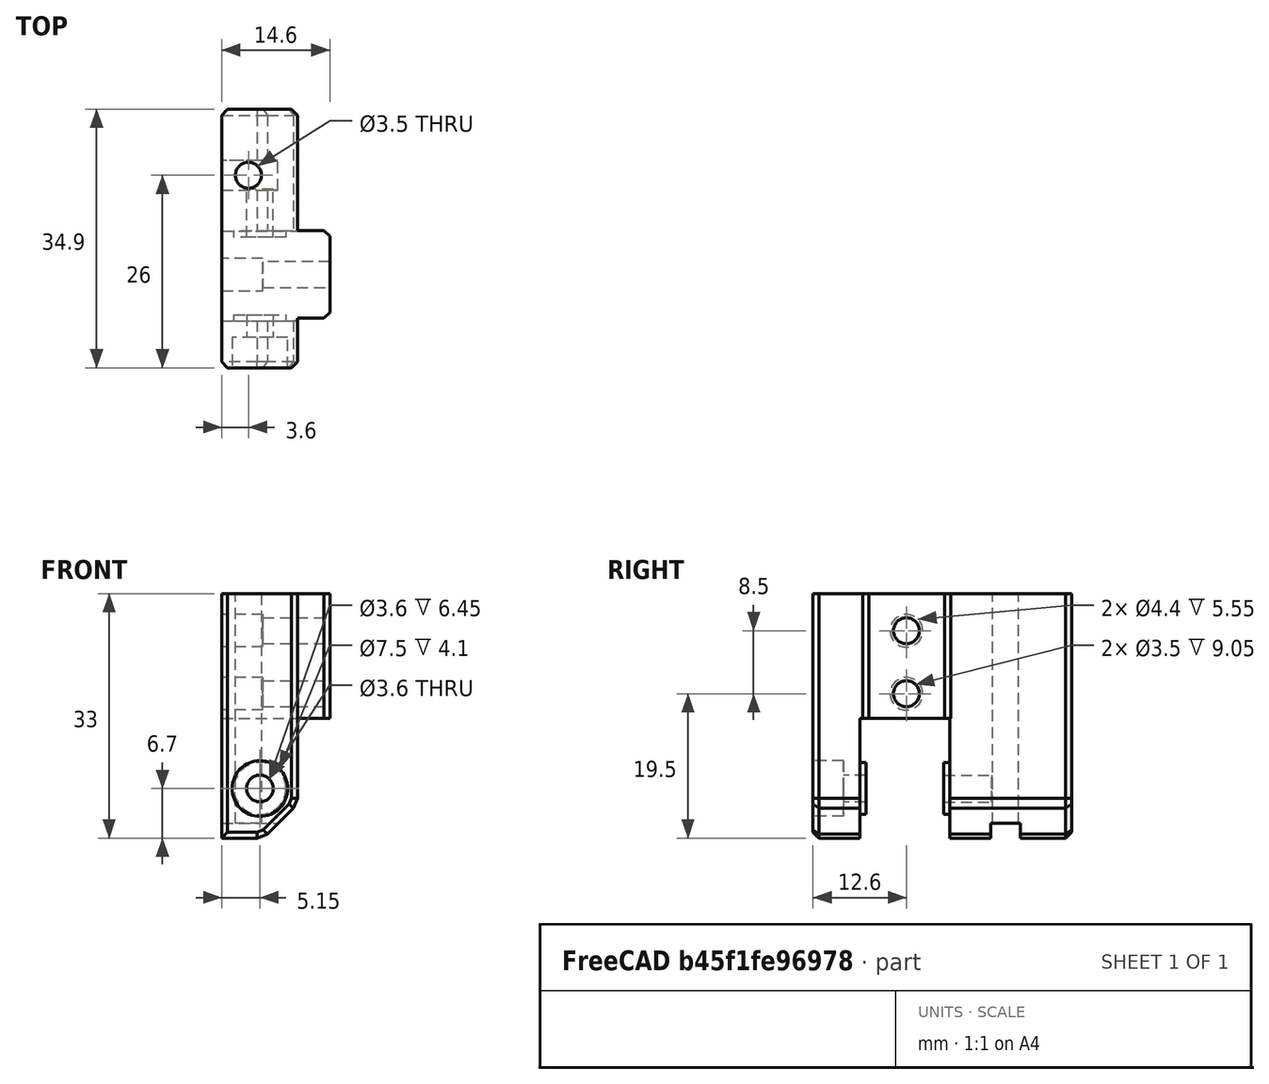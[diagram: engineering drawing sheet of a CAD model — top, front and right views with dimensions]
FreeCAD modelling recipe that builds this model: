
FCSTD DOCUMENT  (FreeCAD 1.0R38641 +468 (Git))
Label: k1_tensioner_right
License: All rights reserved
LicenseURL: https://en.wikipedia.org/wiki/All_rights_reserved
objects: Part::Feature×1, App::Link×1, PartDesign::FeatureBase×1, PartDesign::Body×1, App::Part×1
note: 4 computed .brp shape members not serialized (recipe doc carries the construction recipe); baked Part::Feature solids carry a one-line shape summary decoded from their .brp
EXTERNAL_REF file=cad_powge_pulley.FCStd obj=Part

FEATURE [Part::Feature] Part__Feature  label="step"
  shape: bbox 14.6 x 34.9 x 33 mm, 55 faces (baked)
FEATURE [App::Link] Link  label="cad_powge_pulley_link"
  LinkPlacement = pos=(5.3,-27.85,6.7) rot=(-1,0,0;1.5708rad)
  LinkedObject = -> <external cad_powge_pulley.FCStd>#Part
  Placement = pos=(5.3,-27.85,6.7) rot=(-1,0,0;1.5708rad)
FEATURE [PartDesign::FeatureBase] BaseFeature
  BaseFeature = -> Part__Feature
  Suppressed = false
FEATURE [PartDesign::Body] Body  label="k1_tensioner_right"
  AllowCompound = false
  BaseFeature = -> Part__Feature
  Group = -> [BaseFeature]
  Origin = -> Origin001
  Tip = -> BaseFeature
FEATURE [App::Part] Part  label="k1_tensioner_right_part"
  Group = -> [Body,Link]
  Origin = -> Origin
  Placement = pos=(0,0,0) rot=(0.57735,-0.57735,-0.57735;2.0944rad)

RESOLVED EXTERNAL PARTS (link-assembly join: the EXTERNAL_REF files above that resolve inside this repo's crawl, each included once):
---- part cad_powge_pulley.FCStd = doc fcstd_d49da9a9e340 ----
FCSTD DOCUMENT  (FreeCAD 1.0R38641 +468 (Git))
Label: cad_powge_pulley
License: All rights reserved
LicenseURL: https://en.wikipedia.org/wiki/All_rights_reserved
objects: Sketcher::SketchObject×1, PartDesign::Revolution×1, PartDesign::Body×1, App::Part×1
note: 6 computed .brp shape members not serialized (recipe doc carries the construction recipe); baked Part::Feature solids carry a one-line shape summary decoded from their .brp

FEATURE [Sketcher::SketchObject] Sketch
  ArcFitTolerance = 1e-06
  AttachmentSupport = -> [XZ_Plane]
  FullyConstrained = true
  MakeInternals = false
  MapMode = 5
  Placement = pos=(0,0,0) rot=(1,0,0;1.5708rad)
  sketch-geometry (8):
    g0: LineSegment StartX=6.1 StartY=9.3 StartZ=0 EndX=6.1 EndY=1.2 EndZ=0
    g1: LineSegment StartX=6.1 StartY=1.2 StartZ=0 EndX=8 EndY=1.2 EndZ=0
    g2: LineSegment StartX=8 StartY=1.2 StartZ=0 EndX=8 EndY=0 EndZ=0
    g3: LineSegment StartX=8 StartY=0 StartZ=0 EndX=2 EndY=0 EndZ=0
    g4: LineSegment StartX=2 StartY=0 StartZ=0 EndX=2 EndY=10.5 EndZ=0
    g5: LineSegment StartX=2 StartY=10.5 StartZ=0 EndX=8 EndY=10.5 EndZ=0
    g6: LineSegment StartX=8 StartY=10.5 StartZ=0 EndX=8 EndY=9.3 EndZ=0
    g7: LineSegment StartX=8 StartY=9.3 StartZ=0 EndX=6.1 EndY=9.3 EndZ=0
  constraints (24):
    c: Vertical(g0)
    c: Coincident(g1,g0)
    c: Horizontal(g1)
    c: Coincident(g2,g1)
    c: PointOnObject(g2,g-1)
    c: Vertical(g2)
    c: Coincident(g3,g2)
    c: PointOnObject(g3,g-1)
    c: Coincident(g4,g3)
    c: Vertical(g4)
    c: Coincident(g5,g4)
    c: Horizontal(g5)
    c: Coincident(g6,g5)
    c: Vertical(g6)
    c: Coincident(g7,g6)
    c: Horizontal(g7)
    c: Coincident(g0,g7)
    c: Equal(g5,g3)
    c: Equal(g6,g2)
    c: Distance(g4,g-2) = 2
    c: Distance(g5,g-2) = 8
    c: DistanceY(g0,g0) = 8.1
    c: DistanceY(g4,g4) = 10.5
    c: Distance(g0,g-2) = 6.1
FEATURE [PartDesign::Revolution] Revolution
  Angle = 360
  Angle2 = 60
  Axis = (0,2e-16,1)
  Base = (0,0,0)
  Placement = pos=(0,0,0) rot=(1,0,0;1.5708rad)
  Profile = -> Sketch
  ReferenceAxis = -> Sketch [V_Axis]
  Refine = true
  Reversed = true
  Suppressed = false
  Type = 0
FEATURE [PartDesign::Body] Body  label="powge_pulley"
  AllowCompound = false
  Group = -> [Sketch,Revolution]
  Origin = -> Origin
  Tip = -> Revolution
FEATURE [App::Part] Part  label="powge_pulley_part"
  Group = -> [Body]
  Origin = -> Origin001
